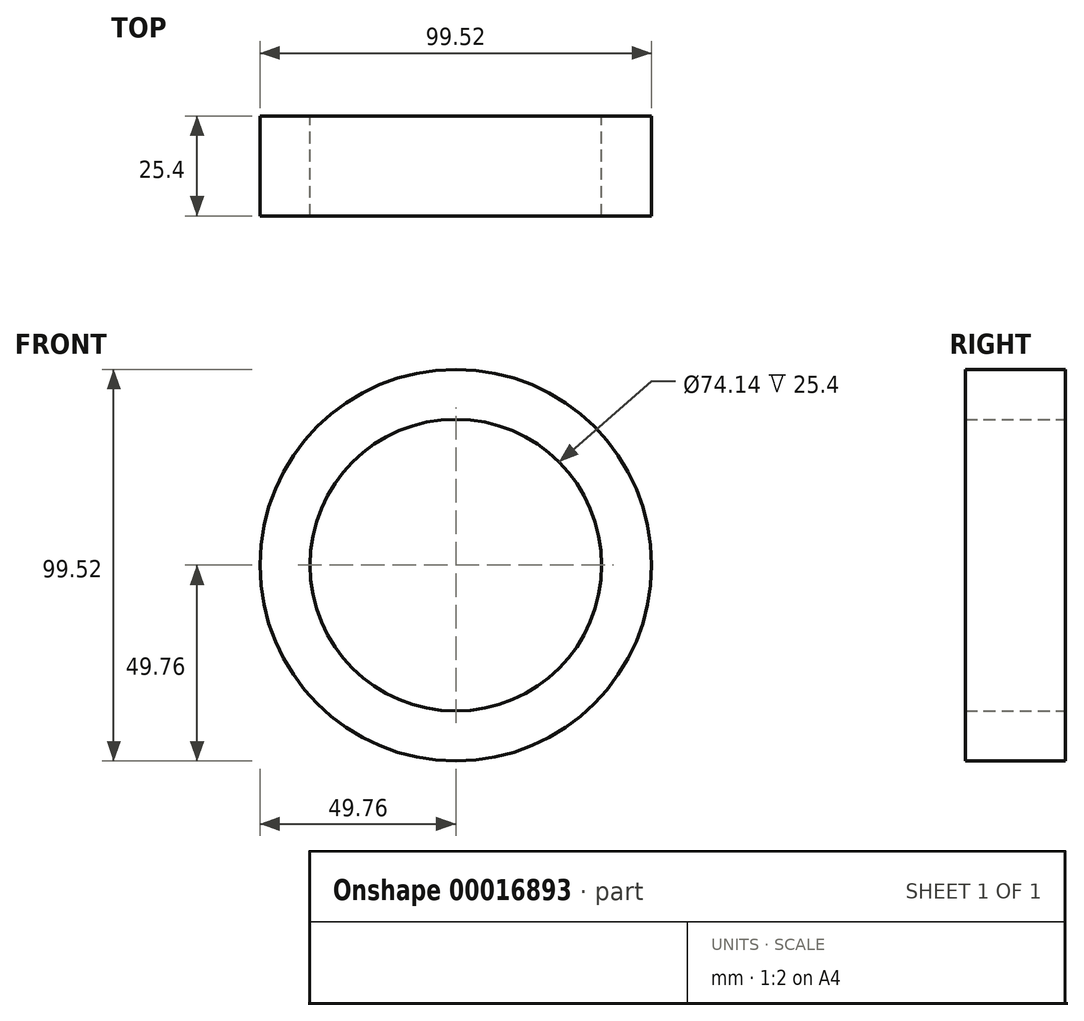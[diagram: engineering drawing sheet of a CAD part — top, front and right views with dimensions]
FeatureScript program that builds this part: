
annotation { "Feature Type Name" : "Feature", "Feature Type Description" : "" }
export const myFeature = defineFeature(function(context is Context, id is Id, definition is map)
    precondition{}
    {
        {
            var Q0;
            Q0=qCreatedBy(makeId("Front.planeOp"),FACE);
            var sketch = newSketch(context, id + "F0", { "sketchPlane" : qUnion([Q0])});
            skCircle(sketch, "E0", {"center": v(0, 0) * mm, "radius": 37.07 * mm});
            skCircle(sketch, "E1", {"center": v(0, 0) * mm, "radius": 49.76 * mm});
            skSolve(sketch);
        }
        {
            var Q0;
            Q0=makeQuery(id+"F0.imprint","IMPRINT",FACE,{"disambiguationData":[TD([[makeQuery(id+"F0.imprint","IMPRINT",EDGE,{"derivedFrom":sQuery(id+"F0.wireOp",EDGE,"E0")}),-1.0]])]});
            extrude(context, id + "F1", {"entities" : qUnion([Q0]), "depth" : 25.4 * mm});
        }
    });
